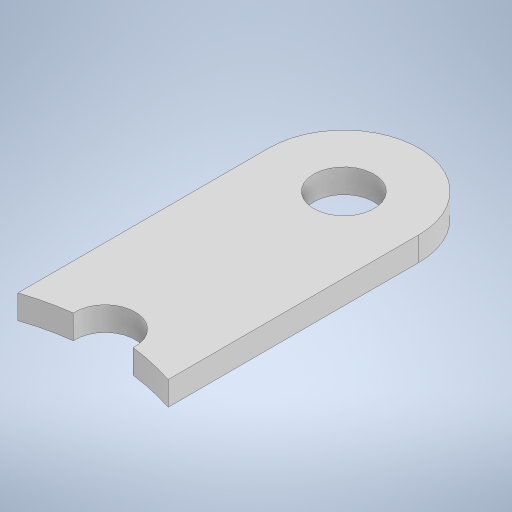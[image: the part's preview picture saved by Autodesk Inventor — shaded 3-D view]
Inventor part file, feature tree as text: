
AUTODESK INVENTOR PART (.ipt)
format: ipt  version: 2024.1 (Build 281209000, 209)  size: 237,056 bytes
history: native  units: mm
features: other x1, extrude x1, sketch x1
ambient origin geometry x8: Origin, YZ Plane, XZ Plane, XY Plane, X Axis, Y Axis, Z Axis, Center Point
bodies: Body1 (feature_tree)
feature tree (3):
  other  "ソリッド1"
  extrude  "押し出し1"  Depth=114.0mm
  sketch  "スケッチ1"
